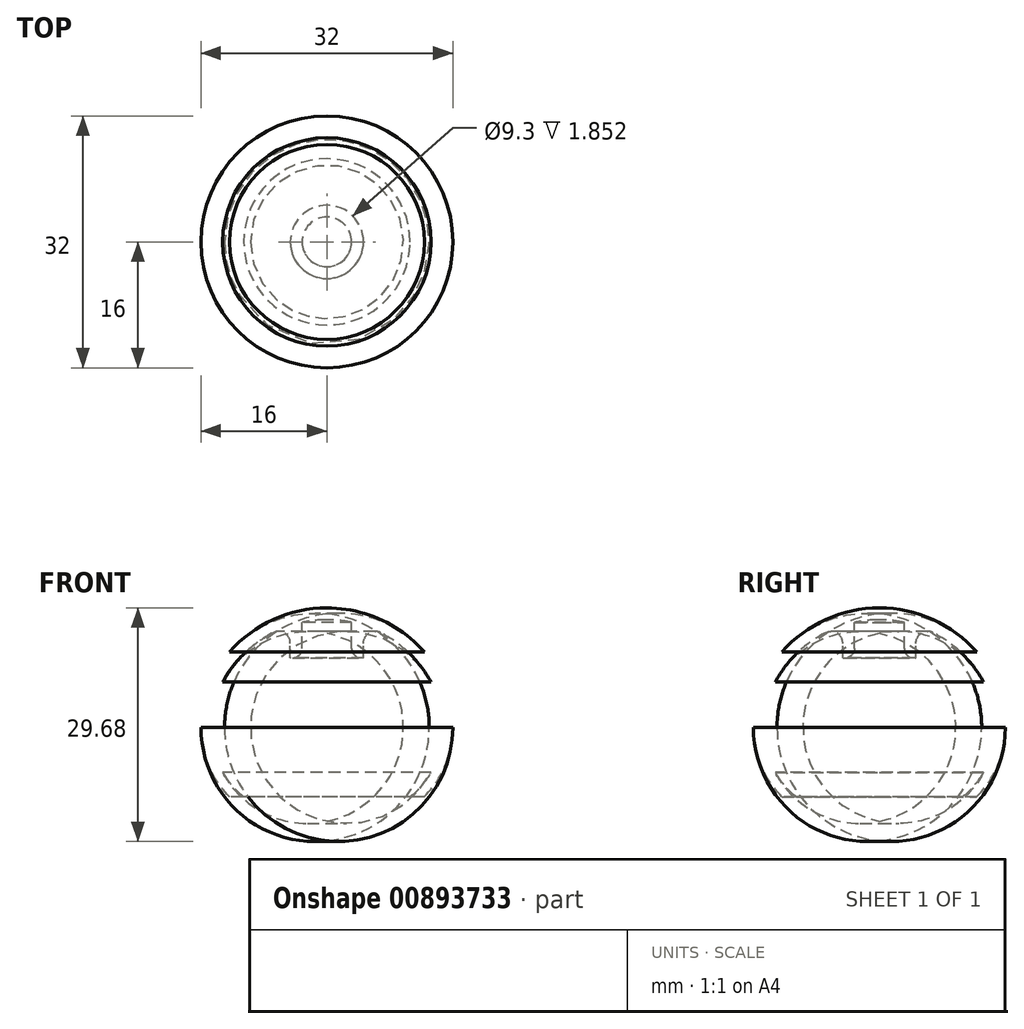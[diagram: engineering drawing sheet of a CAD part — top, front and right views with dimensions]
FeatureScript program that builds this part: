
annotation { "Feature Type Name" : "Feature", "Feature Type Description" : "" }
export const myFeature = defineFeature(function(context is Context, id is Id, definition is map)
    precondition{}
    {
        {
            var Q0;
            Q0=qCreatedBy(makeId("Front.planeOp"),FACE);
            var sketch = newSketch(context, id + "F0", { "sketchPlane" : qUnion([Q0])});
            skLineSegment(sketch, "E0", {"start": v(-4.65, 21.76) * mm, "end": v(-4.65, 17.67) * mm});
            skLineSegment(sketch, "E1", {"start": v(-4.65, 17.67) * mm, "end": v(-3.15, 17.67) * mm});
            skLineSegment(sketch, "E2", {"start": v(-3.15, 17.67) * mm, "end": v(-3.15, 22.17) * mm});
            skArc(sketch, "E3.0", {"start": v(-16, 8.82) * mm, "mid": v(-15.05, 4.05) * mm, "end": v(-12.35, 0) * mm});
            skArc(sketch, "E3.1", {"start": v(-12.37, 18.41) * mm, "mid": v(-15.06, 13.95) * mm, "end": v(-16, 8.82) * mm});
            skArc(sketch, "E3.2", {"start": v(0, 24) * mm, "mid": v(-6.79, 22.54) * mm, "end": v(-12.37, 18.41) * mm});
            skLineSegment(sketch, "E4", {"start": v(-16, 24) * mm, "end": v(-16, 0) * mm, "construction": true});
            skLineSegment(sketch, "E5", {"start": v(-16, 24) * mm, "end": v(0, 24) * mm, "construction": true});
            skArc(sketch, "E6.0", {"start": v(-13.23, 3.08) * mm, "mid": v(-12.03, 1.42) * mm, "end": v(-10.56, 0) * mm});
            skArc(sketch, "E7.0", {"start": v(0, 22.5) * mm, "mid": v(-7.71, 20.37) * mm, "end": v(-13.23, 14.57) * mm});
            skLineSegment(sketch, "E8", {"start": v(0, 24) * mm, "end": v(0, 22.5) * mm});
            skLineSegment(sketch, "E9", {"start": v(-13.23, 14.57) * mm, "end": v(-13.23, 3.08) * mm, "construction": true});
            skPoint(sketch, "E10", {"position": v(-13.23, 8.82) * mm});
            skArc(sketch, "E11", {"start": v(-13.23, 14.57) * mm, "mid": v(-14.67, 8.82) * mm, "end": v(-13.23, 3.08) * mm});
            skLineSegment(sketch, "E12", {"start": v(-12.35, 0) * mm, "end": v(-10.56, 0) * mm});
            skSolve(sketch);
        }
        {
            var Q0;
            Q0=qSketchRegion(id+"F0",true);
            var Q1;
            Q1=sQuery(id+"F0.wireOp",EDGE,"E8");
            revolve(context, id + "F1", {"surfaceOperationType" : NewSurfaceOperationType.NEW, "entities" : qUnion([Q0]), "axis" : qUnion([Q1]), "revolveType" : RevolveType.FULL});
        }
        {
            var Q0;
            Q0=makeQuery(id+"F1.opRevolve","SWEPT_EDGE",EDGE,{"disambiguationData":[OSD([sQuery(id+"F0.wireOp",EDGE,"E1"),sQuery(id+"F0.wireOp",EDGE,"E2")])]});
            fillet(context, id + "F2", {"entities" : qUnion([Q0]), "radius" : 1.2 * mm, "tangentPropagation" : true, "allowEdgeOverflow" : false});
        }
        {
            var Q0;
            Q0=makeQuery(id+"F1.opRevolve","SWEPT_EDGE",EDGE,{"disambiguationData":[OSD([sQuery(id+"F0.wireOp",EDGE,"E0"),sQuery(id+"F0.wireOp",EDGE,"E7.0")])]});
            fillet(context, id + "F3", {"entities" : qUnion([Q0]), "radius" : 1.5 * mm, "tangentPropagation" : true, "allowEdgeOverflow" : false});
        }
    });
